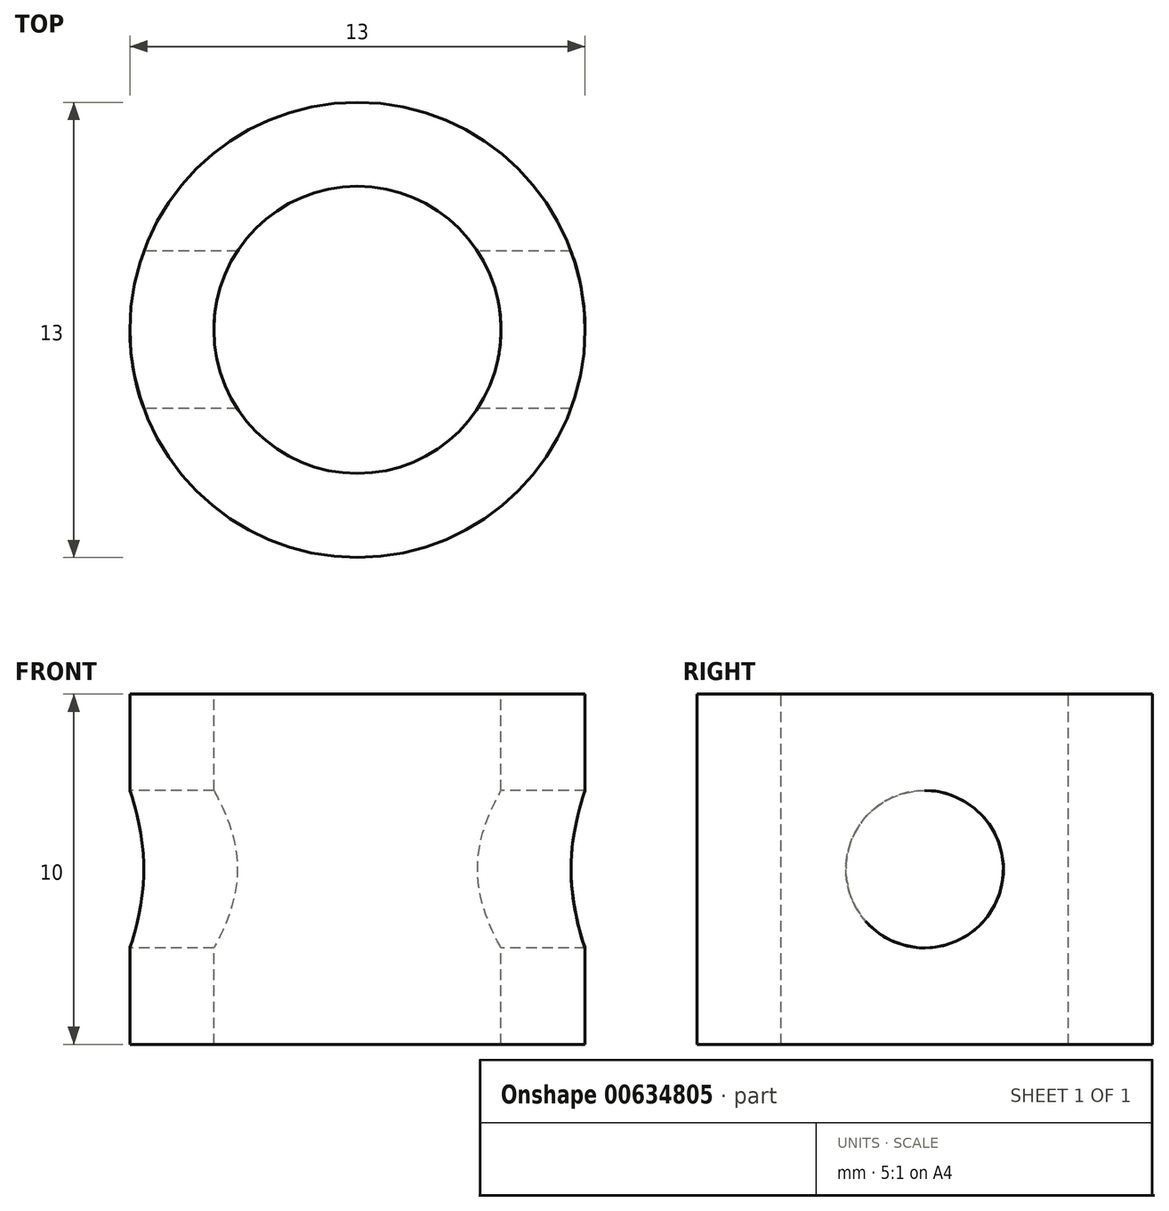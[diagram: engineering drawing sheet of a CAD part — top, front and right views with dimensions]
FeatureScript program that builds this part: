
annotation { "Feature Type Name" : "Feature", "Feature Type Description" : "" }
export const myFeature = defineFeature(function(context is Context, id is Id, definition is map)
    precondition{}
    {
        {
            var Q0;
            Q0=qCreatedBy(makeId("Top.planeOp"),FACE);
            var sketch = newSketch(context, id + "F0", { "sketchPlane" : qUnion([Q0])});
            skCircle(sketch, "E0", {"center": v(0, 0) * mm, "radius": 6.5 * mm});
            skSolve(sketch);
        }
        {
            var Q0;
            Q0=makeQuery(id+"F0.imprint","IMPRINT",FACE,{"disambiguationData":[TD([[makeQuery(id+"F0.imprint","IMPRINT",EDGE,{"derivedFrom":sQuery(id+"F0.wireOp",EDGE,"E0")}),1.0]])]});
            extrude(context, id + "F1", {"entities" : qUnion([Q0]), "depth" : 10 * mm, "offsetDistance" : 25 * mm});
        }
        {
            var Q0;
            Q0=makeQuery(id+"F1.opExtrude","CAP_FACE",FACE,{"disambiguationData":[OSD([sQuery(id+"F0.wireOp",EDGE,"E0")])],"isStart":false});
            var sketch = newSketch(context, id + "F2", { "sketchPlane" : qUnion([Q0])});
            skCircle(sketch, "E1", {"center": v(0, 0) * mm, "radius": 4.1 * mm});
            skSolve(sketch);
        }
        {
            var Q0;
            Q0=makeQuery(id+"F2.imprint","IMPRINT",FACE,{"disambiguationData":[TD([[makeQuery(id+"F2.imprint","IMPRINT",EDGE,{"derivedFrom":sQuery(id+"F2.wireOp",EDGE,"E1")}),1.0]])]});
            extrude(context, id + "F3", {"entities" : qUnion([Q0]), "operationType" : NewBodyOperationType.REMOVE, "oppositeDirection" : true, "depth" : 10 * mm, "offsetDistance" : 25 * mm});
        }
        {
            var Q0;
            Q0=qCreatedBy(makeId("Right.planeOp"),FACE);
            var sketch = newSketch(context, id + "F4", { "sketchPlane" : qUnion([Q0])});
            skCircle(sketch, "E2", {"center": v(0, 5) * mm, "radius": 2.25 * mm});
            skSolve(sketch);
        }
        {
            var Q0;
            Q0=makeQuery(id+"F4.imprint","IMPRINT",FACE,{"disambiguationData":[TD([[makeQuery(id+"F4.imprint","IMPRINT",EDGE,{"derivedFrom":sQuery(id+"F4.wireOp",EDGE,"E2")}),1.0]])]});
            extrude(context, id + "F5", {"entities" : qUnion([Q0]), "operationType" : NewBodyOperationType.REMOVE, "endBound" : BoundingType.SYMMETRIC, "depth" : 25 * mm, "offsetDistance" : 25 * mm});
        }
    });
